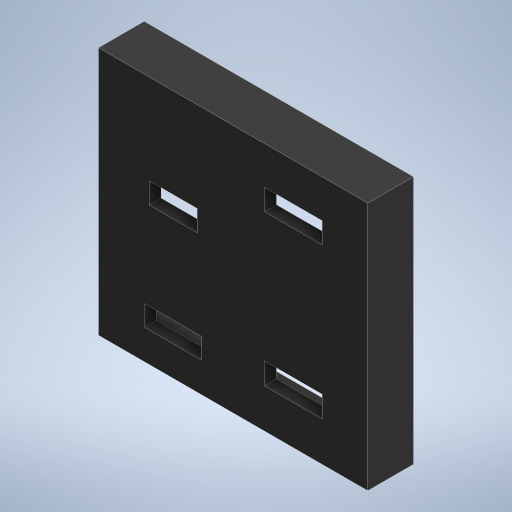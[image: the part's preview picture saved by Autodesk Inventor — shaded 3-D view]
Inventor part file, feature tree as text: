
AUTODESK INVENTOR PART (.ipt)
format: ipt  version: 2024 (Build 280153000, 153)  size: 272,896 bytes
history: native  units: in
note: dims shown in document units (in); Inventor stores cm internally (conversion verified against a paired STEP export)
features: sketch x2, extrude x2, projected_geometry x1
ambient origin geometry x8: Origin, YZ Plane, XZ Plane, XY Plane, X Axis, Y Axis, Z Axis, Center Point
bodies: Solid1 (feature_tree)
feature tree (5):
  sketch  "Sketch1"  dims[d0=0.02in d1=0.02in]
  extrude  "Extrusion1"  Depth=0.02in
  extrude  "Extrusion2"  Depth=0.125in
  sketch  "Sketch3"  dims[d2=0.125in d3=0.125in d4=0.125in d5=0.0in d6=0.125in d7=0.35in d8=0.0in d9=0.6in d10=0.22in d11=90.0deg d13=0.22in d14=0.22in d15=0.6in d16=0.6in d17=0.25in d18=0.225in]
  projected_geometry  "Projected Loop1"
